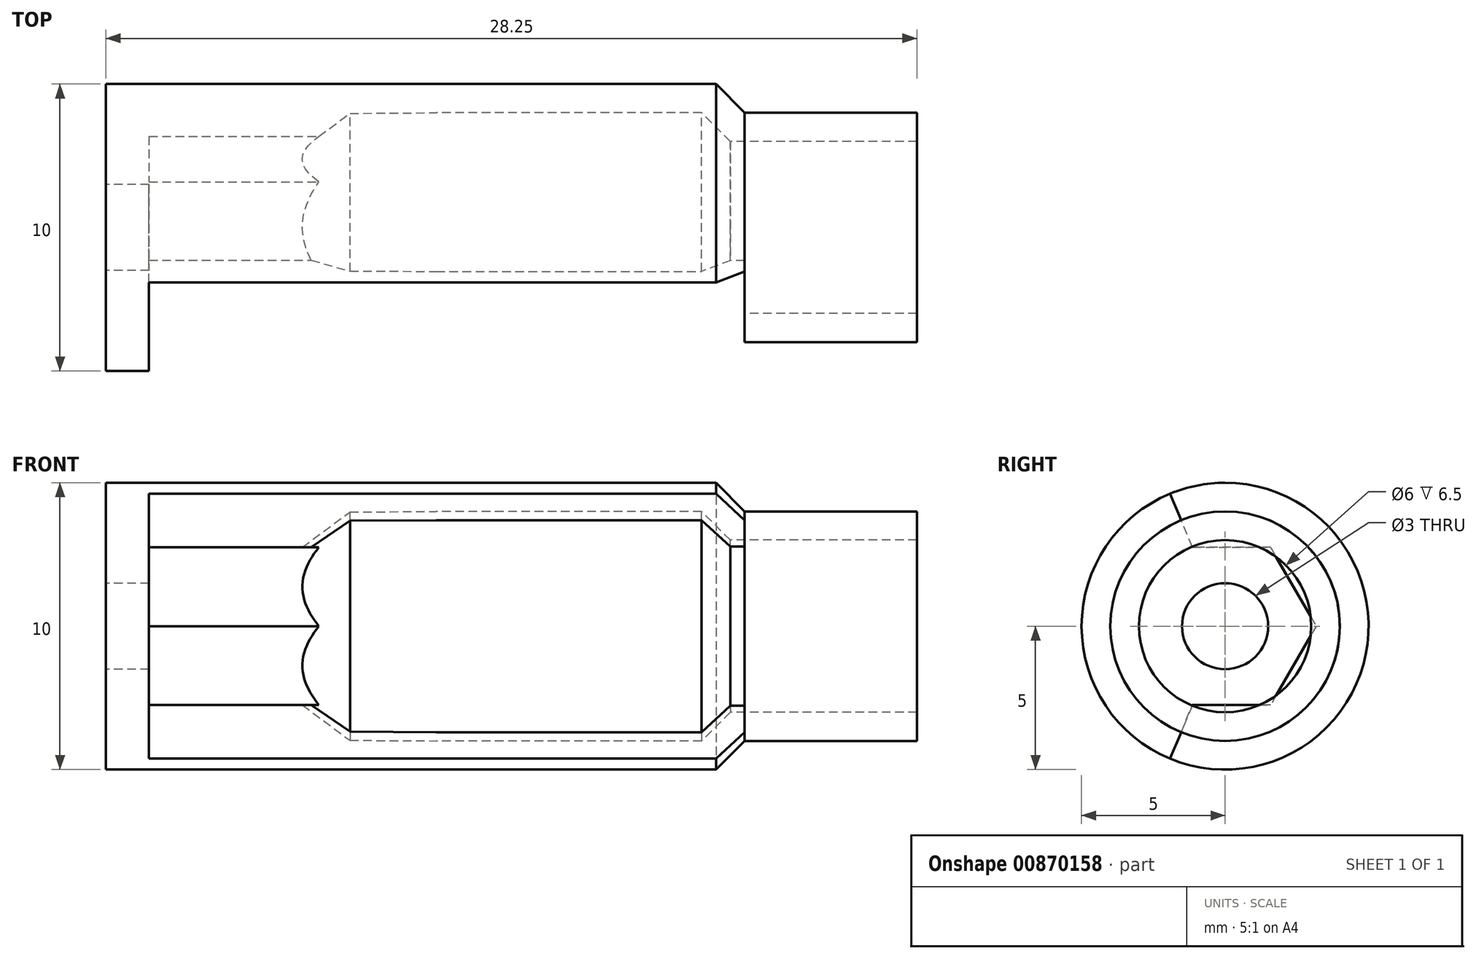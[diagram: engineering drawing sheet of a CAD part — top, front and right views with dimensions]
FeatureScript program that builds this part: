
annotation { "Feature Type Name" : "Feature", "Feature Type Description" : "" }
export const myFeature = defineFeature(function(context is Context, id is Id, definition is map)
    precondition{}
    {
        {
            var Q0;
            Q0=qCreatedBy(makeId("Top.planeOp"),FACE);
            var sketch = newSketch(context, id + "F0", { "sketchPlane" : qUnion([Q0])});
            skLineSegment(sketch, "E0.right", {"start": v(6, 4) * mm, "end": v(6, 3) * mm});
            skLineSegment(sketch, "E1", {"start": v(-8.97, 0) * mm, "end": v(15.16, 0) * mm});
            skLineSegment(sketch, "E2.bottom", {"start": v(-9.75, 5) * mm, "end": v(-19.75, 5) * mm});
            skLineSegment(sketch, "E2.right", {"start": v(-19.75, 5) * mm, "end": v(-19.75, 2.5) * mm});
            skPoint(sketch, "E3.firstSnap0", {"position": v(-19.75, 3.75) * mm});
            skLineSegment(sketch, "E3.bottom", {"start": v(-19.75, 1.5) * mm, "end": v(-21.25, 1.5) * mm});
            skLineSegment(sketch, "E3.top", {"start": v(-19.75, 5) * mm, "end": v(-21.25, 5) * mm});
            skLineSegment(sketch, "E3.left", {"start": v(-19.75, 1.5) * mm, "end": v(-19.75, 5) * mm});
            skLineSegment(sketch, "E3.right", {"start": v(-21.25, 1.5) * mm, "end": v(-21.25, 5) * mm});
            skLineSegment(sketch, "E4.bottom", {"start": v(-21.25, -1.5) * mm, "end": v(-19.75, -1.5) * mm});
            skLineSegment(sketch, "E4.top", {"start": v(-21.25, -5) * mm, "end": v(-19.75, -5) * mm});
            skLineSegment(sketch, "E4.left", {"start": v(-21.25, -1.5) * mm, "end": v(-21.25, -5) * mm});
            skLineSegment(sketch, "E4.right", {"start": v(-19.75, -1.5) * mm, "end": v(-19.75, -5) * mm});
            skLineSegment(sketch, "E5", {"start": v(-9.75, 5) * mm, "end": v(0, 5) * mm});
            skLineSegment(sketch, "E6", {"start": v(0, 5) * mm, "end": v(1, 4) * mm});
            skLineSegment(sketch, "E7", {"start": v(-9.75, 4) * mm, "end": v(-0.5, 4) * mm});
            skLineSegment(sketch, "E8", {"start": v(0.5, 3) * mm, "end": v(-0.5, 4) * mm});
            skLineSegment(sketch, "E9.bottom", {"start": v(6, 4) * mm, "end": v(7, 4) * mm});
            skLineSegment(sketch, "E9.right", {"start": v(7, 4) * mm, "end": v(7, 3) * mm});
            skLineSegment(sketch, "E10.bottom", {"start": v(1, 4) * mm, "end": v(6, 4) * mm});
            skLineSegment(sketch, "E10.top", {"start": v(1, 3) * mm, "end": v(6, 3) * mm});
            skLineSegment(sketch, "E10.left", {"start": v(1, 4) * mm, "end": v(1, 3) * mm});
            skLineSegment(sketch, "E11", {"start": v(1, 3) * mm, "end": v(0.5, 3) * mm});
            skPoint(sketch, "E12", {"position": v(-14.75, 2.5) * mm});
            skLineSegment(sketch, "E13", {"start": v(-19.75, 2.5) * mm, "end": v(-14.75, 2.5) * mm});
            skLineSegment(sketch, "E14", {"start": v(-9.75, 4) * mm, "end": v(-9.75, 5) * mm});
            skLineSegment(sketch, "E15", {"start": v(6, 3) * mm, "end": v(7, 3) * mm});
            skLineSegment(sketch, "E16", {"start": v(-14.75, 2.5) * mm, "end": v(-12.75, 3.98) * mm});
            skLineSegment(sketch, "E17", {"start": v(-12.75, 3.98) * mm, "end": v(-9.75, 4) * mm});
            skSolve(sketch);
        }
        {
            var Q0;
            Q0=makeQuery(id+"F0.imprint","IMPRINT",FACE,{"disambiguationData":[TD([[makeQuery(id+"F0.imprint","IMPRINT",EDGE,{"derivedFrom":sQuery(id+"F0.wireOp",EDGE,"E0.bottom")}),-1.0]])]});
            var Q1;
            Q1=makeQuery(id+"F0.imprint","IMPRINT",FACE,{"disambiguationData":[TD([[makeQuery(id+"F0.imprint","IMPRINT",EDGE,{"derivedFrom":sQuery(id+"F0.wireOp",EDGE,"E2.bottom")}),1.0]])]});
            var Q2;
            Q2=makeQuery(id+"F0.imprint","IMPRINT",FACE,{"disambiguationData":[TD([[makeQuery(id+"F0.imprint","IMPRINT",EDGE,{"derivedFrom":sQuery(id+"F0.wireOp",EDGE,"E5")}),-1.0]])]});
            var Q3;
            Q3=sQuery(id+"F0.wireOp",EDGE,"E1");
            revolve(context, id + "F1", {"surfaceOperationType" : NewSurfaceOperationType.NEW, "entities" : qUnion([Q0, Q1, Q2]), "axis" : qUnion([Q3]), "revolveType" : RevolveType.SYMMETRIC, "angle" : 225 * degree});
        }
        {
            var Q0;
            Q0=qCreatedBy(makeId("Right.planeOp"),FACE);
            cPlane(context, id + "F2", {"entities" : qUnion([Q0]), "cplaneType" : CPlaneType.OFFSET, "offset" : 9.38 * mm, "oppositeDirection" : true, "width" : 150 * mm, "height" : 150 * mm});
        }
        {
            var Q0;
            Q0=qCreatedBy(id+"F2.planeOp",FACE);
            var sketch = newSketch(context, id + "F3", { "sketchPlane" : qUnion([Q0])});
            skCircle(sketch, "E18", {"center": v(0, 0) * mm, "radius": 2.75 * mm});
            skCircle(sketch, "E19.cCircle", {"center": v(0, 0) * mm, "radius": 2.75 * mm, "construction": true});
            skLineSegment(sketch, "E19.0", {"start": v(-1.59, 2.75) * mm, "end": v(1.59, 2.75) * mm});
            skLineSegment(sketch, "E19.1", {"start": v(1.59, 2.75) * mm, "end": v(3.18, 0) * mm});
            skLineSegment(sketch, "E19.2", {"start": v(3.18, 0) * mm, "end": v(1.59, -2.75) * mm});
            skLineSegment(sketch, "E19.3", {"start": v(1.59, -2.75) * mm, "end": v(-1.59, -2.75) * mm});
            skLineSegment(sketch, "E19.4", {"start": v(-1.59, -2.75) * mm, "end": v(-3.18, 0) * mm});
            skLineSegment(sketch, "E19.5", {"start": v(-3.18, 0) * mm, "end": v(-1.59, 2.75) * mm});
            skPoint(sketch, "E19.0.midPoint", {"position": v(0, 2.75) * mm});
            skSolve(sketch);
        }
        {
            var Q0;
            Q0 = qSketchRegion(id + "F3", true);
            extrude(context, id + "F4", {"entities" : qUnion([Q0]), "operationType" : NewBodyOperationType.REMOVE, "oppositeDirection" : true, "depth" : 10.5 * mm, "offsetDistance" : 25 * mm});
        }
        {
            var Q0;
            Q0=makeQuery(id+"F0.imprint","IMPRINT",FACE,{"disambiguationData":[TD([[makeQuery(id+"F0.imprint","IMPRINT",EDGE,{"derivedFrom":sQuery(id+"F0.wireOp",EDGE,"E2.right")}),-1.0]])]});
            var Q1;
            Q1=makeQuery(id+"F0.imprint","IMPRINT",FACE,{"disambiguationData":[TD([[makeQuery(id+"F0.imprint","IMPRINT",EDGE,{"derivedFrom":sQuery(id+"F0.wireOp",EDGE,"E4.bottom")}),-1.0]])]});
            var Q2;
            Q2=sQuery(id+"F0.wireOp",EDGE,"E1");
            revolve(context, id + "F5", {"operationType" : NewBodyOperationType.ADD, "surfaceOperationType" : NewSurfaceOperationType.NEW, "entities" : qUnion([Q0, Q1]), "axis" : qUnion([Q2]), "revolveType" : RevolveType.FULL});
        }
        {
            var Q0;
            Q0=makeQuery(id+"F0.imprint","IMPRINT",FACE,{"disambiguationData":[TD([[makeQuery(id+"F0.imprint","IMPRINT",EDGE,{"derivedFrom":sQuery(id+"F0.wireOp",EDGE,"E0.right")}),1.0]])]});
            var Q1;
            Q1=makeQuery(id+"F0.imprint","IMPRINT",FACE,{"disambiguationData":[TD([[makeQuery(id+"F0.imprint","IMPRINT",EDGE,{"derivedFrom":sQuery(id+"F0.wireOp",EDGE,"E0.right")}),-1.0]])]});
            var Q2;
            Q2=sQuery(id+"F0.wireOp",EDGE,"E1");
            revolve(context, id + "F6", {"operationType" : NewBodyOperationType.ADD, "surfaceOperationType" : NewSurfaceOperationType.NEW, "entities" : qUnion([Q0, Q1]), "axis" : qUnion([Q2]), "revolveType" : RevolveType.FULL});
        }
    });
